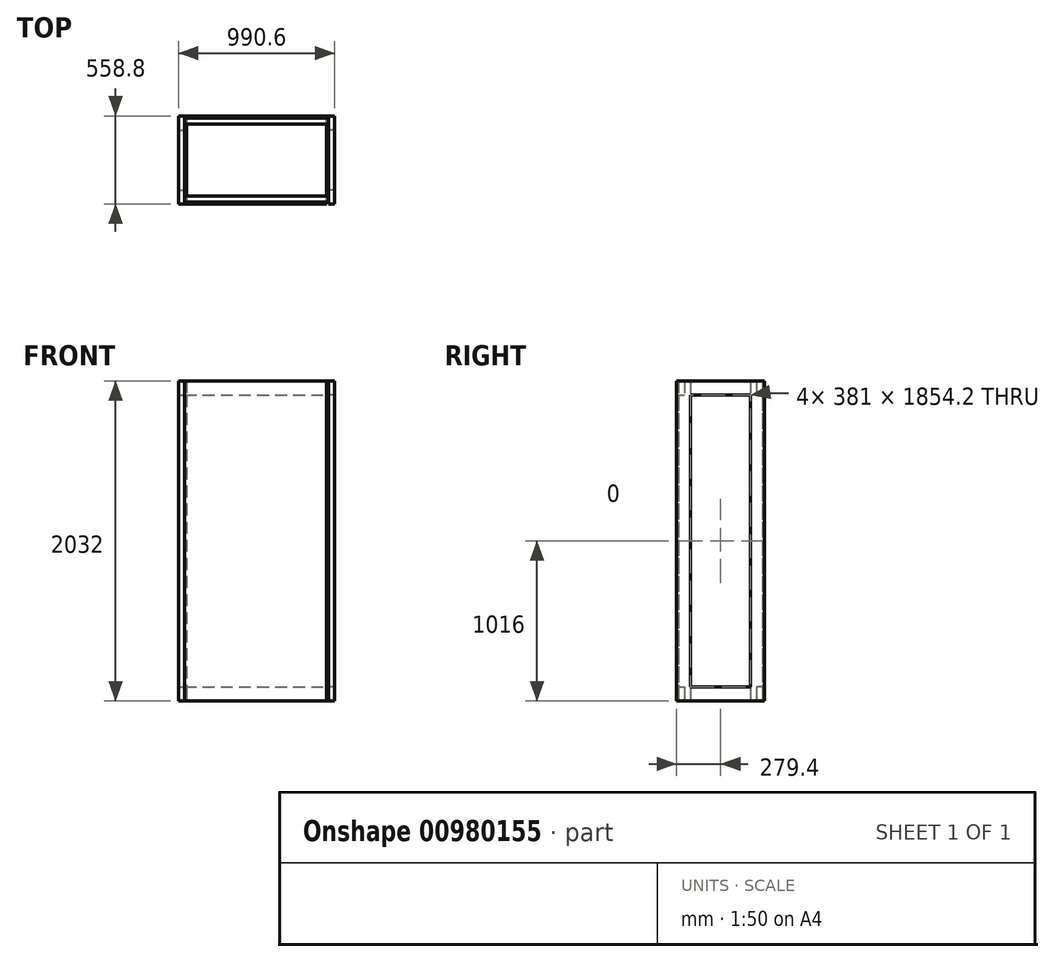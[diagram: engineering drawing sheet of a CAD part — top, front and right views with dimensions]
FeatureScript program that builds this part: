
annotation { "Feature Type Name" : "Feature", "Feature Type Description" : "" }
export const myFeature = defineFeature(function(context is Context, id is Id, definition is map)
    precondition{}
    {
        {
            var Q0;
            Q0=qCreatedBy(makeId("Front.planeOp"),FACE);
            var sketch = newSketch(context, id + "F0", { "sketchPlane" : qUnion([Q0])});
            skLineSegment(sketch, "E0.bottom", {"start": v(457.2, 1016) * mm, "end": v(-457.2, 1016) * mm});
            skLineSegment(sketch, "E0.top", {"start": v(457.2, -1016) * mm, "end": v(-457.2, -1016) * mm});
            skLineSegment(sketch, "E0.left", {"start": v(457.2, 1016) * mm, "end": v(457.2, -1016) * mm});
            skLineSegment(sketch, "E0.right", {"start": v(-457.2, 1016) * mm, "end": v(-457.2, -1016) * mm});
            skPoint(sketch, "E0.middle", {"position": v(0, 0) * mm});
            skSolve(sketch);
        }
        {
            var Q0;
            Q0=makeQuery(id+"F0.imprint","IMPRINT",FACE,{"disambiguationData":[TD([[makeQuery(id+"F0.imprint","IMPRINT",EDGE,{"derivedFrom":sQuery(id+"F0.wireOp",EDGE,"E0.bottom")}),1.0]])]});
            extrude(context, id + "F1", {"entities" : qUnion([Q0]), "endBound" : BoundingType.SYMMETRIC, "depth" : 558.8 * mm, "offsetDistance" : 25.4 * mm});
        }
        {
            var Q0;
            Q0=makeQuery(id+"F1.opExtrude","SWEPT_FACE",FACE,{"disambiguationData":[OSD([sQuery(id+"F0.wireOp",EDGE,"E0.left")])]});
            var sketch = newSketch(context, id + "F2", { "sketchPlane" : qUnion([Q0])});
            skLineSegment(sketch, "E1.bottom", {"start": v(-279.4, 1016) * mm, "end": v(-190.5, 1016) * mm});
            skLineSegment(sketch, "E1.top", {"start": v(-279.4, -1016) * mm, "end": v(-190.5, -1016) * mm});
            skLineSegment(sketch, "E1.left", {"start": v(-279.4, 1016) * mm, "end": v(-279.4, -1016) * mm});
            skLineSegment(sketch, "E1.right", {"start": v(-190.5, 1016) * mm, "end": v(-190.5, -1016) * mm});
            skLineSegment(sketch, "E2.MirrorCS", {"start": v(190.5, 1016) * mm, "end": v(190.5, -1016) * mm});
            skLineSegment(sketch, "E3.MirrorCS", {"start": v(279.4, 1016) * mm, "end": v(279.4, -1016) * mm});
            skLineSegment(sketch, "E4.MirrorCS", {"start": v(279.4, 1016) * mm, "end": v(190.5, 1016) * mm});
            skLineSegment(sketch, "E5.MirrorCS", {"start": v(279.4, -1016) * mm, "end": v(190.5, -1016) * mm});
            skLineSegment(sketch, "E6.bottom", {"start": v(-190.5, 1016) * mm, "end": v(190.5, 1016) * mm});
            skLineSegment(sketch, "E6.top", {"start": v(-190.5, 927.1) * mm, "end": v(190.5, 927.1) * mm});
            skLineSegment(sketch, "E6.left", {"start": v(-190.5, 1016) * mm, "end": v(-190.5, 927.1) * mm});
            skLineSegment(sketch, "E6.right", {"start": v(190.5, 1016) * mm, "end": v(190.5, 927.1) * mm});
            skLineSegment(sketch, "E7.MirrorCS", {"start": v(-190.5, -927.1) * mm, "end": v(190.5, -927.1) * mm});
            skLineSegment(sketch, "E8.MirrorCS", {"start": v(-190.5, -1016) * mm, "end": v(-190.5, -927.1) * mm});
            skLineSegment(sketch, "E9.MirrorCS", {"start": v(-190.5, -1016) * mm, "end": v(190.5, -1016) * mm});
            skLineSegment(sketch, "E10.MirrorCS", {"start": v(190.5, -1016) * mm, "end": v(190.5, -927.1) * mm});
            skSolve(sketch);
        }
        {
            var Q0;
            Q0=makeQuery(id+"F2.imprint","IMPRINT",FACE,{"disambiguationData":[TD([[makeQuery(id+"F2.imprint","IMPRINT",EDGE,{"derivedFrom":sQuery(id+"F2.wireOp",EDGE,"E2.MirrorCS")}),1.0]])]});
            var Q1;
            Q1=makeQuery(id+"F2.imprint","IMPRINT",FACE,{"disambiguationData":[TD([[makeQuery(id+"F2.imprint","IMPRINT",EDGE,{"derivedFrom":sQuery(id+"F2.wireOp",EDGE,"E6.bottom")}),-1.0]])]});
            var Q2;
            Q2=makeQuery(id+"F2.imprint","IMPRINT",FACE,{"disambiguationData":[TD([[makeQuery(id+"F2.imprint","IMPRINT",EDGE,{"derivedFrom":sQuery(id+"F2.wireOp",EDGE,"E1.bottom")}),-1.0]])]});
            var Q3;
            Q3=makeQuery(id+"F2.imprint","IMPRINT",FACE,{"disambiguationData":[TD([[makeQuery(id+"F2.imprint","IMPRINT",EDGE,{"derivedFrom":sQuery(id+"F2.wireOp",EDGE,"E7.MirrorCS")}),-1.0]])]});
            extrude(context, id + "F3", {"entities" : qUnion([Q0, Q1, Q2, Q3]), "depth" : 38.1 * mm, "offsetDistance" : 25.4 * mm});
        }
        {
            var Q0;
            Q0=makeQuery(id+"F3.opExtrude","SWEPT_BODY",BODY,{"disambiguationData":[OSD([sQuery(id+"F2.wireOp",EDGE,"E1.bottom"),sQuery(id+"F2.wireOp",EDGE,"E1.top"),sQuery(id+"F2.wireOp",EDGE,"E1.left"),sQuery(id+"F2.wireOp",EDGE,"E1.right"),sQuery(id+"F2.wireOp",EDGE,"E2.MirrorCS"),sQuery(id+"F2.wireOp",EDGE,"E3.MirrorCS"),sQuery(id+"F2.wireOp",EDGE,"E4.MirrorCS"),sQuery(id+"F2.wireOp",EDGE,"E5.MirrorCS"),sQuery(id+"F2.wireOp",EDGE,"E6.bottom"),sQuery(id+"F2.wireOp",EDGE,"E6.top"),sQuery(id+"F2.wireOp",EDGE,"E7.MirrorCS"),sQuery(id+"F2.wireOp",EDGE,"E9.MirrorCS")])]});
            var Q1;
            Q1=qCreatedBy(makeId("Right.planeOp"),FACE);
            mirror(context, id + "F4", {"entities" : qUnion([Q0]), "mirrorPlane" : qUnion([Q1])});
        }
        {
            var Q0;
            Q0=makeQuery(id+"F4.opPattern","COPY",FACE,{"derivedFrom":makeQuery(id+"F3.opExtrude","SWEPT_FACE",FACE,{"disambiguationData":[OSD([sQuery(id+"F2.wireOp",EDGE,"E1.left")])]}),"instanceName":"1"});
            var sketch = newSketch(context, id + "F5", { "sketchPlane" : qUnion([Q0])});
            skLineSegment(sketch, "E11.0", {"start": v(457.2, 1016) * mm, "end": v(457.2, -1016) * mm});
            skLineSegment(sketch, "E12.0", {"start": v(-457.2, 1016) * mm, "end": v(-457.2, -1016) * mm});
            skLineSegment(sketch, "E13.bottom", {"start": v(-457.2, 1016) * mm, "end": v(457.2, 1016) * mm});
            skLineSegment(sketch, "E13.top", {"start": v(-457.2, 927.1) * mm, "end": v(457.2, 927.1) * mm});
            skLineSegment(sketch, "E13.left", {"start": v(-457.2, 1016) * mm, "end": v(-457.2, 927.1) * mm});
            skLineSegment(sketch, "E13.right", {"start": v(457.2, 1016) * mm, "end": v(457.2, 927.1) * mm});
            skLineSegment(sketch, "E14.MirrorCS", {"start": v(-457.2, -927.1) * mm, "end": v(457.2, -927.1) * mm});
            skLineSegment(sketch, "E15.MirrorCS", {"start": v(-457.2, -1016) * mm, "end": v(457.2, -1016) * mm});
            skLineSegment(sketch, "E16.MirrorCS", {"start": v(457.2, -1016) * mm, "end": v(457.2, 1016) * mm});
            skSolve(sketch);
        }
        {
            var Q0;
            {var subQ0=sQuery(id+"F5.wireOp",EDGE,"E13.bottom");Q0=makeQuery(id+"F5.imprint","IMPRINT",FACE,{"disambiguationData":[TD([[makeQuery(id+"F5.imprint","IMPRINT",EDGE,{"derivedFrom":subQ0}),-1.0]])]});}
            var Q1;
            {var subQ2=sQuery(id+"F5.wireOp",EDGE,"E14.MirrorCS");Q1=makeQuery(id+"F5.imprint","IMPRINT",FACE,{"disambiguationData":[TD([[makeQuery(id+"F5.imprint","IMPRINT",EDGE,{"derivedFrom":subQ2}),-1.0]])]});}
            extrude(context, id + "F6", {"entities" : qUnion([Q0, Q1]), "oppositeDirection" : true, "depth" : 38.1 * mm, "offsetDistance" : 25.4 * mm});
        }
        {
            var Q0;
            Q0=makeQuery(id+"F6.opExtrude","SWEPT_BODY",BODY,{"disambiguationData":[OSD([sQuery(id+"F5.wireOp",EDGE,"E13.bottom"),sQuery(id+"F5.wireOp",EDGE,"E13.top"),sQuery(id+"F5.wireOp",EDGE,"E13.left"),sQuery(id+"F5.wireOp",EDGE,"E16.MirrorCS")])]});
            var Q1;
            Q1=makeQuery(id+"F6.opExtrude","SWEPT_BODY",BODY,{"disambiguationData":[OSD([sQuery(id+"F5.wireOp",EDGE,"E12.0"),sQuery(id+"F5.wireOp",EDGE,"E14.MirrorCS"),sQuery(id+"F5.wireOp",EDGE,"E15.MirrorCS"),sQuery(id+"F5.wireOp",EDGE,"E16.MirrorCS")])]});
            transform(context, id + "F7", {"entities" : qUnion([Q0, Q1]), "transformType" : TransformType.TRANSLATION_3D, "dx" : 0 * mm, "dy" : 12.7 * mm, "dz" : 0 * mm, "makeCopy" : false});
        }
        {
            var Q0;
            Q0=makeQuery(id+"F6.opExtrude","SWEPT_BODY",BODY,{"disambiguationData":[OSD([sQuery(id+"F5.wireOp",EDGE,"E13.bottom"),sQuery(id+"F5.wireOp",EDGE,"E13.top"),sQuery(id+"F5.wireOp",EDGE,"E13.left"),sQuery(id+"F5.wireOp",EDGE,"E16.MirrorCS")])]});
            var Q1;
            Q1=makeQuery(id+"F6.opExtrude","SWEPT_BODY",BODY,{"disambiguationData":[OSD([sQuery(id+"F5.wireOp",EDGE,"E12.0"),sQuery(id+"F5.wireOp",EDGE,"E14.MirrorCS"),sQuery(id+"F5.wireOp",EDGE,"E15.MirrorCS"),sQuery(id+"F5.wireOp",EDGE,"E16.MirrorCS")])]});
            transform(context, id + "F8", {"entities" : qUnion([Q0, Q1]), "transformType" : TransformType.TRANSLATION_3D, "dx" : 0 * mm, "dy" : 495.3 * mm, "dz" : 0 * mm, "makeCopy" : true});
        }
        {
            var Q0;
            Q0=makeQuery(id+"F3.opExtrude","CAP_FACE",FACE,{"disambiguationData":[OSD([sQuery(id+"F2.wireOp",EDGE,"E1.bottom"),sQuery(id+"F2.wireOp",EDGE,"E1.top"),sQuery(id+"F2.wireOp",EDGE,"E1.left"),sQuery(id+"F2.wireOp",EDGE,"E1.right"),sQuery(id+"F2.wireOp",EDGE,"E2.MirrorCS"),sQuery(id+"F2.wireOp",EDGE,"E3.MirrorCS"),sQuery(id+"F2.wireOp",EDGE,"E4.MirrorCS"),sQuery(id+"F2.wireOp",EDGE,"E5.MirrorCS"),sQuery(id+"F2.wireOp",EDGE,"E6.bottom"),sQuery(id+"F2.wireOp",EDGE,"E6.top"),sQuery(id+"F2.wireOp",EDGE,"E7.MirrorCS"),sQuery(id+"F2.wireOp",EDGE,"E9.MirrorCS")])],"isStart":true});
            var Q1;
            Q1=makeQuery(id+"F2.imprint","IMPRINT",FACE,{"disambiguationData":[TD([[makeQuery(id+"F2.imprint","IMPRINT",EDGE,{"derivedFrom":sQuery(id+"F2.wireOp",EDGE,"E1.right")}),1.0]])]});
            extrude(context, id + "F9", {"entities" : qUnion([Q0, Q1]), "depth" : 12.7 * mm, "offsetDistance" : 25.4 * mm});
        }
        {
            var Q0;
            Q0=makeQuery(id+"F8.opPattern","COPY",BODY,{"derivedFrom":makeQuery(id+"F6.opExtrude","SWEPT_BODY",BODY,{"disambiguationData":[OSD([sQuery(id+"F5.wireOp",EDGE,"E13.bottom"),sQuery(id+"F5.wireOp",EDGE,"E13.top"),sQuery(id+"F5.wireOp",EDGE,"E13.left"),sQuery(id+"F5.wireOp",EDGE,"E16.MirrorCS")])]}),"instanceName":"1"});
            var Q1;
            Q1=makeQuery(id+"F6.opExtrude","SWEPT_BODY",BODY,{"disambiguationData":[OSD([sQuery(id+"F5.wireOp",EDGE,"E12.0"),sQuery(id+"F5.wireOp",EDGE,"E14.MirrorCS"),sQuery(id+"F5.wireOp",EDGE,"E15.MirrorCS"),sQuery(id+"F5.wireOp",EDGE,"E16.MirrorCS")])]});
            var Q2;
            Q2=makeQuery(id+"F6.opExtrude","SWEPT_BODY",BODY,{"disambiguationData":[OSD([sQuery(id+"F5.wireOp",EDGE,"E13.bottom"),sQuery(id+"F5.wireOp",EDGE,"E13.top"),sQuery(id+"F5.wireOp",EDGE,"E13.left"),sQuery(id+"F5.wireOp",EDGE,"E16.MirrorCS")])]});
            var Q3;
            Q3=makeQuery(id+"F8.opPattern","COPY",BODY,{"derivedFrom":makeQuery(id+"F6.opExtrude","SWEPT_BODY",BODY,{"disambiguationData":[OSD([sQuery(id+"F5.wireOp",EDGE,"E12.0"),sQuery(id+"F5.wireOp",EDGE,"E14.MirrorCS"),sQuery(id+"F5.wireOp",EDGE,"E15.MirrorCS"),sQuery(id+"F5.wireOp",EDGE,"E16.MirrorCS")])]}),"instanceName":"1"});
            var Q4;
            Q4=makeQuery(id+"F9.opExtrude","SWEPT_BODY",BODY,{"disambiguationData":[OSD([sQuery(id+"F2.wireOp",EDGE,"E1.bottom"),sQuery(id+"F2.wireOp",EDGE,"E1.top"),sQuery(id+"F2.wireOp",EDGE,"E1.left"),sQuery(id+"F2.wireOp",EDGE,"E1.right"),sQuery(id+"F2.wireOp",EDGE,"E2.MirrorCS"),sQuery(id+"F2.wireOp",EDGE,"E3.MirrorCS"),sQuery(id+"F2.wireOp",EDGE,"E4.MirrorCS"),sQuery(id+"F2.wireOp",EDGE,"E5.MirrorCS"),sQuery(id+"F2.wireOp",EDGE,"E6.bottom"),sQuery(id+"F2.wireOp",EDGE,"E6.top"),sQuery(id+"F2.wireOp",EDGE,"E7.MirrorCS"),sQuery(id+"F2.wireOp",EDGE,"E9.MirrorCS")])]});
            booleanBodies(context, id + "F10", {"operationType" : BooleanOperationType.SUBTRACTION, "tools" : qUnion([Q0, Q1, Q2, Q3]), "targets" : qUnion([Q4]), "keepTools" : true});
        }
        {
            var Q0;
            Q0=makeQuery(id+"F9.opExtrude","SWEPT_FACE",FACE,{"disambiguationData":[OSD([sQuery(id+"F2.wireOp",EDGE,"E3.MirrorCS")])]});
            extrude(context, id + "F11", {"entities" : qUnion([Q0]), "operationType" : NewBodyOperationType.REMOVE, "oppositeDirection" : true, "depth" : 12.7 * mm, "offsetDistance" : 25.4 * mm});
        }
        {
            var Q0;
            Q0=makeQuery(id+"F9.opExtrude","SWEPT_FACE",FACE,{"disambiguationData":[OSD([sQuery(id+"F2.wireOp",EDGE,"E1.left")])]});
            extrude(context, id + "F12", {"entities" : qUnion([Q0]), "operationType" : NewBodyOperationType.REMOVE, "oppositeDirection" : true, "depth" : 12.7 * mm, "offsetDistance" : 25.4 * mm});
        }
        {
            var Q0;
            Q0=makeQuery(id+"F9.opExtrude","SWEPT_BODY",BODY,{"disambiguationData":[OSD([sQuery(id+"F2.wireOp",EDGE,"E1.right"),sQuery(id+"F2.wireOp",EDGE,"E2.MirrorCS"),sQuery(id+"F2.wireOp",EDGE,"E6.top"),sQuery(id+"F2.wireOp",EDGE,"E7.MirrorCS")])]});
            transform(context, id + "F13", {"entities" : qUnion([Q0]), "transformType" : TransformType.TRANSLATION_3D, "dx" : -901.7 * mm, "dy" : 0 * mm, "dz" : 0 * mm, "makeCopy" : true});
        }
        {
            var Q0;
            Q0=makeQuery(id+"F8.opPattern","COPY",FACE,{"derivedFrom":makeQuery(id+"F6.opExtrude","CAP_FACE",FACE,{"disambiguationData":[OSD([sQuery(id+"F5.wireOp",EDGE,"E13.bottom"),sQuery(id+"F5.wireOp",EDGE,"E13.top"),sQuery(id+"F5.wireOp",EDGE,"E13.left"),sQuery(id+"F5.wireOp",EDGE,"E16.MirrorCS")])],"isStart":false}),"instanceName":"1"});
            var sketch = newSketch(context, id + "F14", { "sketchPlane" : qUnion([Q0])});
            skPoint(sketch, "E17.0", {"position": v(457.2, 1016) * mm});
            skPoint(sketch, "E18.0", {"position": v(-457.2, -1016) * mm});
            skLineSegment(sketch, "E19.bottom", {"start": v(-457.2, -1016) * mm, "end": v(457.2, -1016) * mm});
            skLineSegment(sketch, "E19.top", {"start": v(-457.2, 1016) * mm, "end": v(457.2, 1016) * mm});
            skLineSegment(sketch, "E19.left", {"start": v(-457.2, -1016) * mm, "end": v(-457.2, 1016) * mm});
            skLineSegment(sketch, "E19.right", {"start": v(457.2, -1016) * mm, "end": v(457.2, 1016) * mm});
            skSolve(sketch);
        }
        {
            var Q0;
            {var subQ0=sQuery(id+"F14.wireOp",EDGE,"E19.bottom");Q0=makeQuery(id+"F14.imprint","IMPRINT",FACE,{"disambiguationData":[TD([[makeQuery(id+"F14.imprint","IMPRINT",EDGE,{"derivedFrom":subQ0}),1.0]])]});}
            var Q1;
            {var subQ0=sQuery(id+"F14.wireOp",EDGE,"E19.top");Q1=makeQuery(id+"F14.imprint","IMPRINT",FACE,{"disambiguationData":[TD([[makeQuery(id+"F14.imprint","IMPRINT",EDGE,{"derivedFrom":subQ0}),1.0]])]});}
            extrude(context, id + "F15", {"entities" : qUnion([Q0, Q1]), "depth" : 12.7 * mm, "offsetDistance" : 25.4 * mm});
        }
    });
